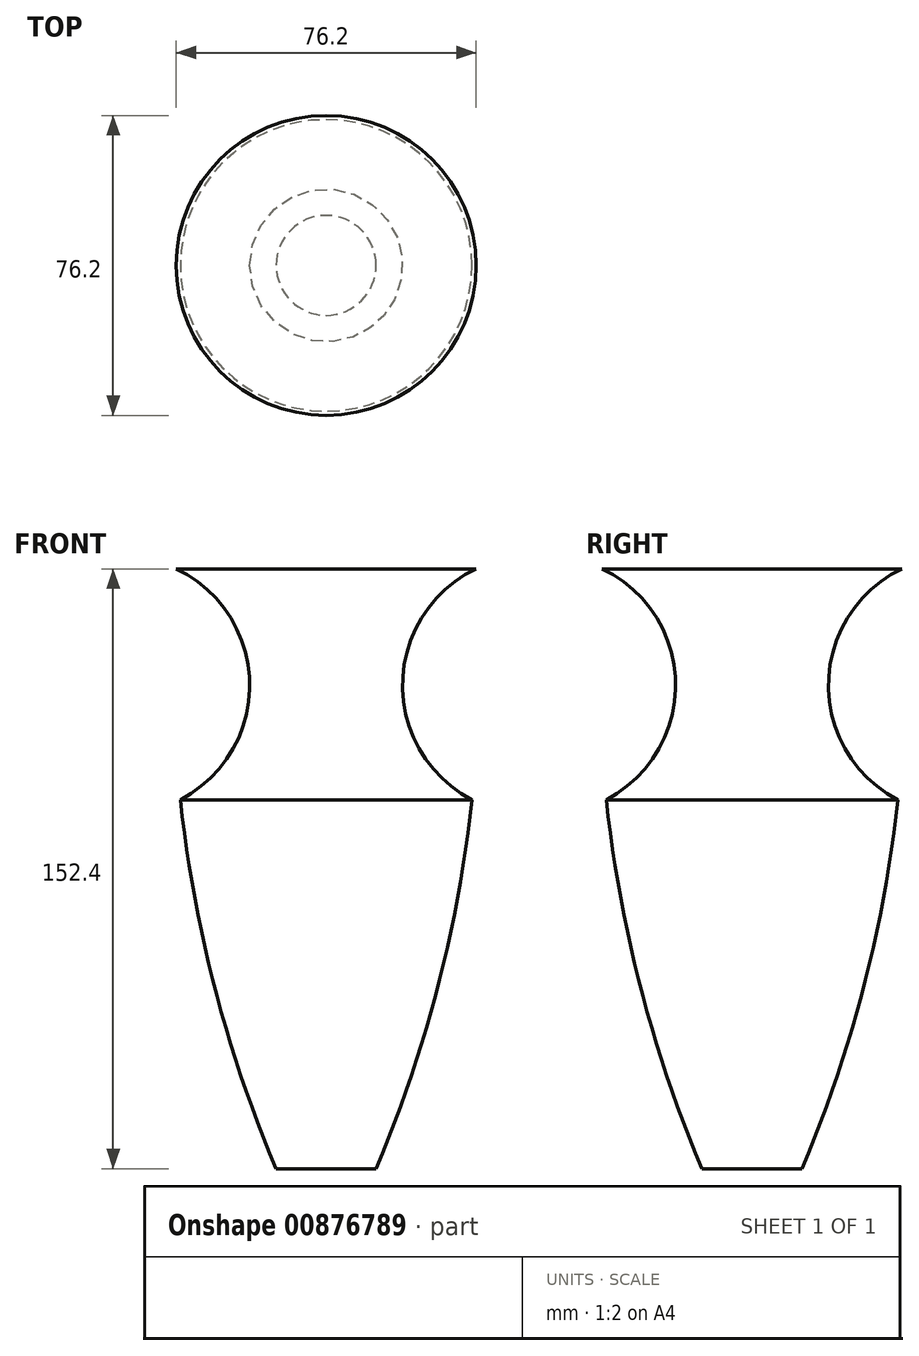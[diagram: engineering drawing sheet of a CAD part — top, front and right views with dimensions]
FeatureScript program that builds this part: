
annotation { "Feature Type Name" : "Feature", "Feature Type Description" : "" }
export const myFeature = defineFeature(function(context is Context, id is Id, definition is map)
    precondition{}
    {
        {
            var Q0;
            Q0=qCreatedBy(makeId("Front.planeOp"),FACE);
            var sketch = newSketch(context, id + "F0", { "sketchPlane" : qUnion([Q0])});
            skLineSegment(sketch, "E0", {"start": v(-38.1, 86.29) * mm, "end": v(38.1, 86.29) * mm});
            skLineSegment(sketch, "E1", {"start": v(0, -66.11) * mm, "end": v(12.7, -66.11) * mm});
            skLineSegment(sketch, "E2", {"start": v(12.7, -66.11) * mm, "end": v(0, -66.11) * mm});
            skLineSegment(sketch, "E3", {"start": v(0, -66.11) * mm, "end": v(-12.7, -66.11) * mm});
            skArc(sketch, "E4", {"start": v(-38.1, 86.29) * mm, "mid": v(-34.42, 8.59) * mm, "end": v(-12.7, -66.11) * mm});
            skArc(sketch, "E5", {"start": v(12.7, -66.11) * mm, "mid": v(34.42, 8.59) * mm, "end": v(38.1, 86.29) * mm});
            skArc(sketch, "E6", {"start": v(-37.02, 27.63) * mm, "mid": v(-19.41, 57.3) * mm, "end": v(-38.1, 86.29) * mm});
            skLineSegment(sketch, "E7", {"start": v(0, -112.1) * mm, "end": v(0, 103.45) * mm});
            skSolve(sketch);
        }
        {
            var Q0;
            {var subQ1=sQuery(id+"F0.wireOp",EDGE,"E3");Q0=makeQuery(id+"F0.imprint","IMPRINT",FACE,{"disambiguationData":[TD([[makeQuery(id+"F0.imprint","IMPRINT",EDGE,{"derivedFrom":subQ1}),-1.0]])]});}
            var Q1;
            Q1=sQuery(id+"F0.wireOp",EDGE,"E7");
            revolve(context, id + "F1", {"surfaceOperationType" : NewSurfaceOperationType.NEW, "entities" : qUnion([Q0]), "axis" : qUnion([Q1]), "revolveType" : RevolveType.FULL});
        }
    });
